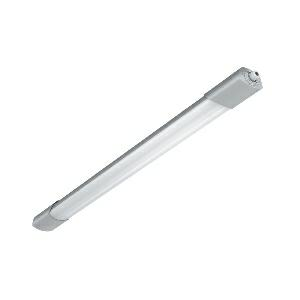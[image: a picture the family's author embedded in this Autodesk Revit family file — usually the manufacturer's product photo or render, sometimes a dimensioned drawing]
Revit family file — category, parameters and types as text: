
# Revit family: rs_pro_connect_5100_led_052911
name_source: partatom
category: Leuchten
revit_build: Autodesk Revit 2016 (Build: 20190508_0715(x64)
units: mm (PartAtom-declared; Revit-internal decimal feet)

## family parameters
Basisbauteil = Fläche
Beim Laden mit Abzugskörper schneiden = Nein
Bemaßung runder Anschluss = Durchmesser verwenden
Gemeinsam genutzt = Nein
Lichtquelle = Nein
Raumberechnungspunkt = Nein
Teiletyp = Normal

## types (1)
- RS PRO Connect 5100 LED (1 x , 4206 lm, 4000 K)
    Beschreibung = Dimensions (L x W x H): 58 x 1370 x 87 mm; Mains power supply: 220 – 240 V / 50 – 60 Hz; Sensor Technology: High frequency; Transmitter power: < 1 mW; HF-system: 5,8 GHz; Output: 30 W; Interconnection: Yes; Type of interconnection: Master/master, Master/slave; Luminous flux: 4206 lm; Colour temperature: 4000 K; Colour variation LED: SDCM3; Colour Rendering Index CRI: 80-89; With lamp: Yes, STEINEL LED system; Lamp: LED cannot be replaced; LED life expectancy (max. °C): 60000 h; Drop in luminous flux in accordance with LM80: L80B10; Base: without; LED cooling system: Passive Thermo Control; With motion detector: Yes; Detection: also through glass, wood and stud walls; Detection angle: 360 °; Angle of aperture: 160 °; Capability of masking out individual segments: Yes; Electronic scalability: Yes; Mechanical scalability: No; Reach, radial: Ø 10 m (79 m²); Reach, tangential: Ø 10 m (79 m²); Main light adjustable: 50 - 100 %; Continuous light: selectable; Photo-cell controller: Yes; Twilight setting: 2 – 2000 lx; Time setting: 5 sec – 60 min; Basic light level function: Yes; Basic light level function time: 10-30 min, all night; Functions: Group parameterisation, Manual ON / ON-OFF, Master/slave override, Neighbouring-group function, Presence function; Soft light start: No; Impact resistance: IK07; IP-rating: IP66; Protection class: II; Ambient temperature: -20 – 40 °C; Housing material: Plastic; Cover material: Plastic, structured; Manufacturer's Warranty: 5 years; Settings via: Bluetooth; With remote control: No; Version: Sensor; PU1, EAN: 4007841052911
    CIE Flux Codes = 48 78 94 98 100
    Color Rendering = 80-89
    Color Temperature = 4000 K
    Frequency = 60 Hz, 50 Hz
    Height = 87 mm
    Hersteller = Steinel
    Lamp Light Flux = 4206 lm
    Lamp count = 1
    Lampe = 1 x
    Length = 58 mm
    Luminous efficacy = 140 lm/W
    ModVariant = Nein
    Modell = 052911
    Mounting Type = Surface mounted
    Number of Poles = 1
    OnlyDefault = Ja
    Power Factor = 1
    Product Name = RS PRO Connect 5100 LED
    Product group = Sensor-switched indoor light
    ProductGroupID = 30
    Protection Class = Protection class II
    Protection Degree = Degree of protection
    RlxData = <blob elided: 58029 chars, md5=c23e2be3>
    Scheinlast = 30 VA
    Socket = socket
    Standby Power = 0 W
    System Light Flux = 4206 lm
    System Power = 30 W
    Typenbild = produkt1_052911.jpg
    Typenkommentare = Product without accessories
    URL = http://relux.com
    VarID = ---
    Voltage = 0 V
    Vorgabe-Ansicht = 1800 mm
    Weight = 0.00 kg
    Width = 1370 mm

## geometry (parser evidence)
native form markers: Blend x4, Sweep x13
no freeform markers — native parametric forms only
